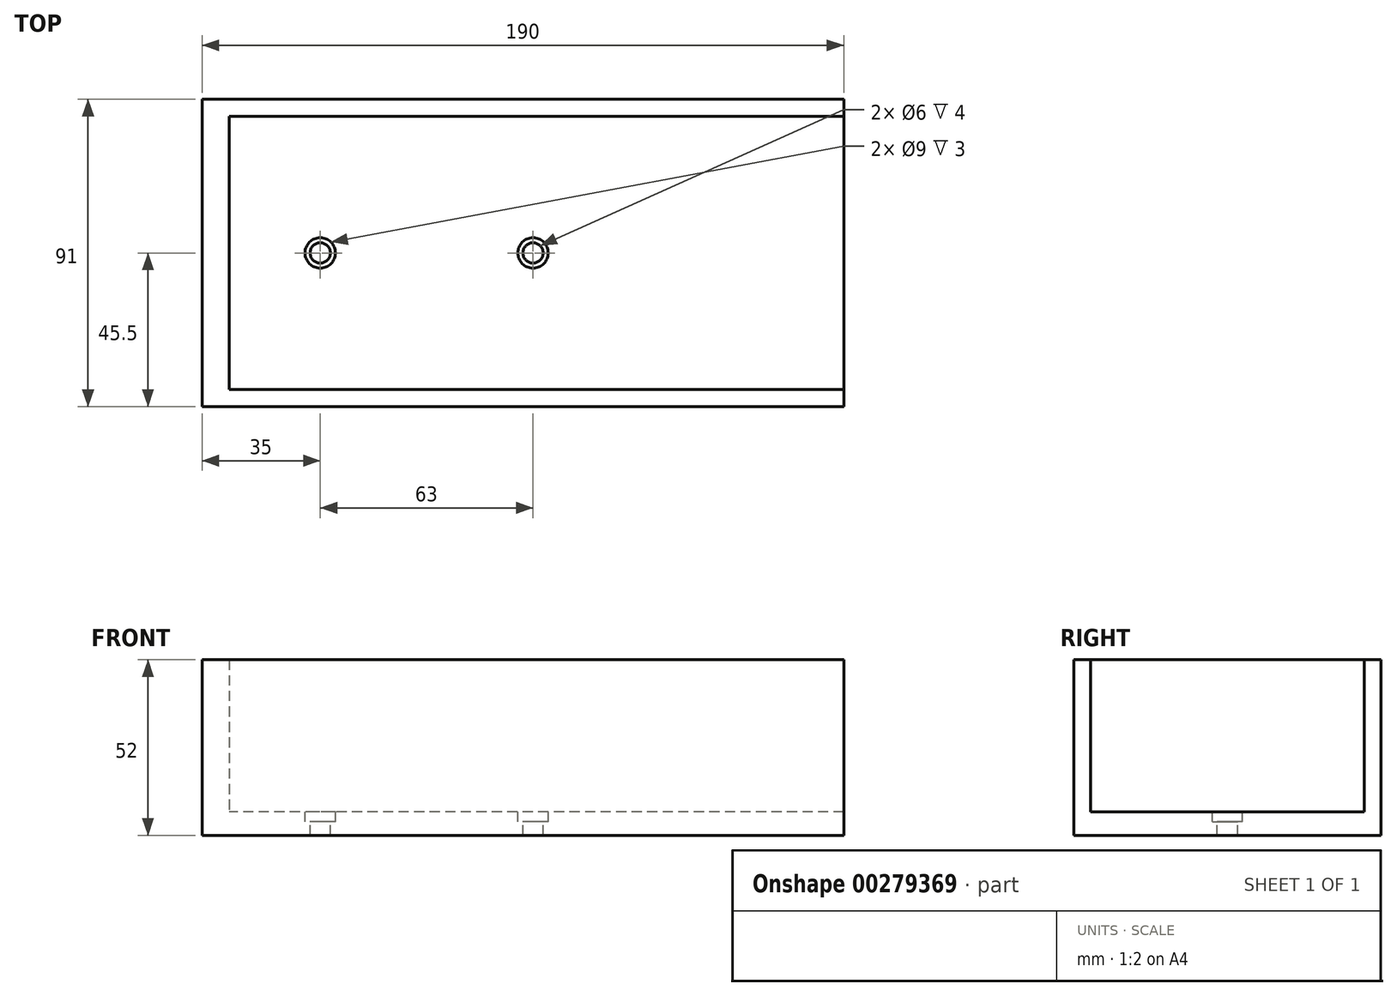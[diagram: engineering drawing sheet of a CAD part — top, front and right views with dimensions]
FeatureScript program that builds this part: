
annotation { "Feature Type Name" : "Feature", "Feature Type Description" : "" }
export const myFeature = defineFeature(function(context is Context, id is Id, definition is map)
    precondition{}
    {
        {
            var Q0;
            Q0=qCreatedBy(makeId("Right.planeOp"),FACE);
            var sketch = newSketch(context, id + "F0", { "sketchPlane" : qUnion([Q0])});
            skLineSegment(sketch, "E0.0", {"start": v(-40.5, -20) * mm, "end": v(-0.5, -20) * mm});
            skLineSegment(sketch, "E1.0", {"start": v(-40.5, 25) * mm, "end": v(-40.5, -20) * mm});
            skLineSegment(sketch, "E2.MirrorCS", {"start": v(40.5, 25) * mm, "end": v(40.5, -20) * mm});
            skLineSegment(sketch, "E3.MirrorCS", {"start": v(40.5, -20) * mm, "end": v(0.5, -20) * mm});
            skLineSegment(sketch, "E4.1", {"start": v(-45.5, 25) * mm, "end": v(-45.5, -27) * mm});
            skLineSegment(sketch, "E4.2", {"start": v(45.5, 25) * mm, "end": v(45.5, -27) * mm});
            skLineSegment(sketch, "E4.3", {"start": v(45.5, 25) * mm, "end": v(40.5, 25) * mm});
            skLineSegment(sketch, "E4.4", {"start": v(-45.5, 25) * mm, "end": v(-40.5, 25) * mm});
            skLineSegment(sketch, "E5.0", {"start": v(-45.5, -27) * mm, "end": v(45.5, -27) * mm});
            skLineSegment(sketch, "E6", {"start": v(0.5, -20) * mm, "end": v(-0.5, -20) * mm});
            skSolve(sketch);
        }
        {
            var Q0;
            Q0=makeQuery(id+"F0.imprint","IMPRINT",FACE,{"disambiguationData":[TD([[makeQuery(id+"F0.imprint","IMPRINT",EDGE,{"derivedFrom":sQuery(id+"F0.wireOp",EDGE,"E0.0")}),-1.0]])]});
            extrude(context, id + "F1", {"entities" : qUnion([Q0]), "depth" : 182 * mm, "offsetDistance" : 25 * mm});
        }
        {
            var Q0;
            Q0=makeQuery(id+"F1.opExtrude","CAP_FACE",FACE,{"disambiguationData":[OSD([sQuery(id+"F0.wireOp",EDGE,"E0.0"),sQuery(id+"F0.wireOp",EDGE,"E1.0"),sQuery(id+"F0.wireOp",EDGE,"E2.MirrorCS"),sQuery(id+"F0.wireOp",EDGE,"E3.MirrorCS"),sQuery(id+"F0.wireOp",EDGE,"E4.1"),sQuery(id+"F0.wireOp",EDGE,"E4.2"),sQuery(id+"F0.wireOp",EDGE,"E4.3"),sQuery(id+"F0.wireOp",EDGE,"E4.4"),sQuery(id+"F0.wireOp",EDGE,"E5.0")])],"isStart":true});
            var sketch = newSketch(context, id + "F2", { "sketchPlane" : qUnion([Q0])});
            skLineSegment(sketch, "E7.0", {"start": v(-45.5, 25) * mm, "end": v(-45.5, -27) * mm});
            skLineSegment(sketch, "E8.0", {"start": v(45.5, 25) * mm, "end": v(45.5, -27) * mm});
            skLineSegment(sketch, "E9.0", {"start": v(45.5, -27) * mm, "end": v(-45.5, -27) * mm});
            skLineSegment(sketch, "E10", {"start": v(-45.5, 25) * mm, "end": v(45.5, 25) * mm});
            skSolve(sketch);
        }
        {
            var Q0;
            Q0 = qSketchRegion(id + "F2", true);
            extrude(context, id + "F3", {"entities" : qUnion([Q0]), "operationType" : NewBodyOperationType.ADD, "depth" : 8 * mm, "offsetDistance" : 25 * mm});
        }
        {
            var Q0;
            Q0=makeQuery(id+"F1.opExtrude","SWEPT_FACE",FACE,{"disambiguationData":[OSD([sQuery(id+"F0.wireOp",EDGE,"E0.0"),sQuery(id+"F0.wireOp",EDGE,"E3.MirrorCS")])]});
            var sketch = newSketch(context, id + "F4", { "sketchPlane" : qUnion([Q0])});
            skLineSegment(sketch, "E11.0", {"start": v(0, 40.5) * mm, "end": v(0, -40.5) * mm});
            skLineSegment(sketch, "E12.0", {"start": v(27, 40) * mm, "end": v(27, -40) * mm});
            skLineSegment(sketch, "E13.0", {"start": v(90, 40) * mm, "end": v(90, -40) * mm});
            skCircle(sketch, "E14", {"center": v(27, 0) * mm, "radius": 3 * mm});
            skCircle(sketch, "E15", {"center": v(90, 0) * mm, "radius": 3 * mm});
            skSolve(sketch);
        }
        {
            var Q0;
            Q0 = qSketchRegion(id + "F4", true);
            extrude(context, id + "F5", {"entities" : qUnion([Q0]), "operationType" : NewBodyOperationType.REMOVE, "oppositeDirection" : true, "depth" : 25 * mm, "offsetDistance" : 25 * mm});
        }
        {
            var Q0;
            Q0=makeQuery(id+"F1.opExtrude","SWEPT_FACE",FACE,{"disambiguationData":[OSD([sQuery(id+"F0.wireOp",EDGE,"E0.0"),sQuery(id+"F0.wireOp",EDGE,"E3.MirrorCS")])]});
            var sketch = newSketch(context, id + "F6", { "sketchPlane" : qUnion([Q0])});
            skCircle(sketch, "E16", {"center": v(27, 0) * mm, "radius": 4.5 * mm});
            skCircle(sketch, "E17", {"center": v(90, 0) * mm, "radius": 4.5 * mm});
            skSolve(sketch);
        }
        {
            var Q0;
            Q0 = qSketchRegion(id + "F6", true);
            extrude(context, id + "F7", {"entities" : qUnion([Q0]), "operationType" : NewBodyOperationType.REMOVE, "oppositeDirection" : true, "depth" : 3 * mm, "offsetDistance" : 25 * mm});
        }
    });
